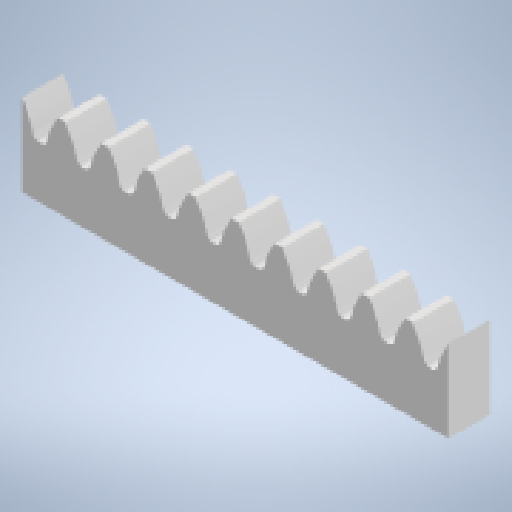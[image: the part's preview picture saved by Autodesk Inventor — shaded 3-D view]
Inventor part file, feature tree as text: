
AUTODESK INVENTOR PART (.ipt)
format: ipt  version: 2023 (Build 270158000, 158)  size: 195,584 bytes
history: native  units: mm
features: extrude x3, sketch x1, pattern_linear x1
ambient origin geometry x8: Origin, YZ Plane, XZ Plane, XY Plane, X Axis, Y Axis, Z Axis, Center Point
bodies: Body1 (feature_tree)
feature tree (5):
  sketch  "Sketch1"  dims[d7=61.768mm d9=2.0mm d10=2.0mm d11=1.0mm d12=5.5mm d13=1.0mm d14=6.5mm d15=0.0mm d16=2.0mm d17=0.0mm d18=0.0mm d19=0.0mm d20=100.0mm d22=6.283mm]
  extrude  "Extrusion3"  Depth=2.0mm
  extrude  "Extrusion4"  Depth=2.0mm
  extrude  "Extrusion5"  Depth=1.0mm
  pattern_linear  "Rectangular Pattern2"  Spacing1=5.5mm  [1 undecoded]
note: 1 required parameter value undecoded (feature->parameter linkage not recoverable at this tier; creation-order binding heuristic only, values carry confidence <= 0.55)
